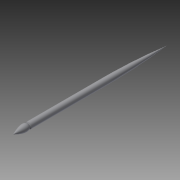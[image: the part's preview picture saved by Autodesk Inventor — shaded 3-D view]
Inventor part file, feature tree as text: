
AUTODESK INVENTOR PART (.ipt)
format: ipt  version: 2013 (Build 170138000, 138)  size: 84,992 bytes
history: native  units: mm
features: revolve x1, sketch x1
ambient origin geometry x8: Origin, YZ Plane, XZ Plane, XY Plane, X Axis, Y Axis, Z Axis, Center Point
bodies: Solid1 (feature_tree)
feature tree (2):
  revolve  "Revolution1"  [1 undecoded]
  sketch  "Sketch1"  dims[d1=200.0mm d2=8.0mm d3=100.0mm d4=20.0mm d5=90.0deg]
note: 1 required parameter value undecoded (feature->parameter linkage not recoverable at this tier; creation-order binding heuristic only, values carry confidence <= 0.55)
